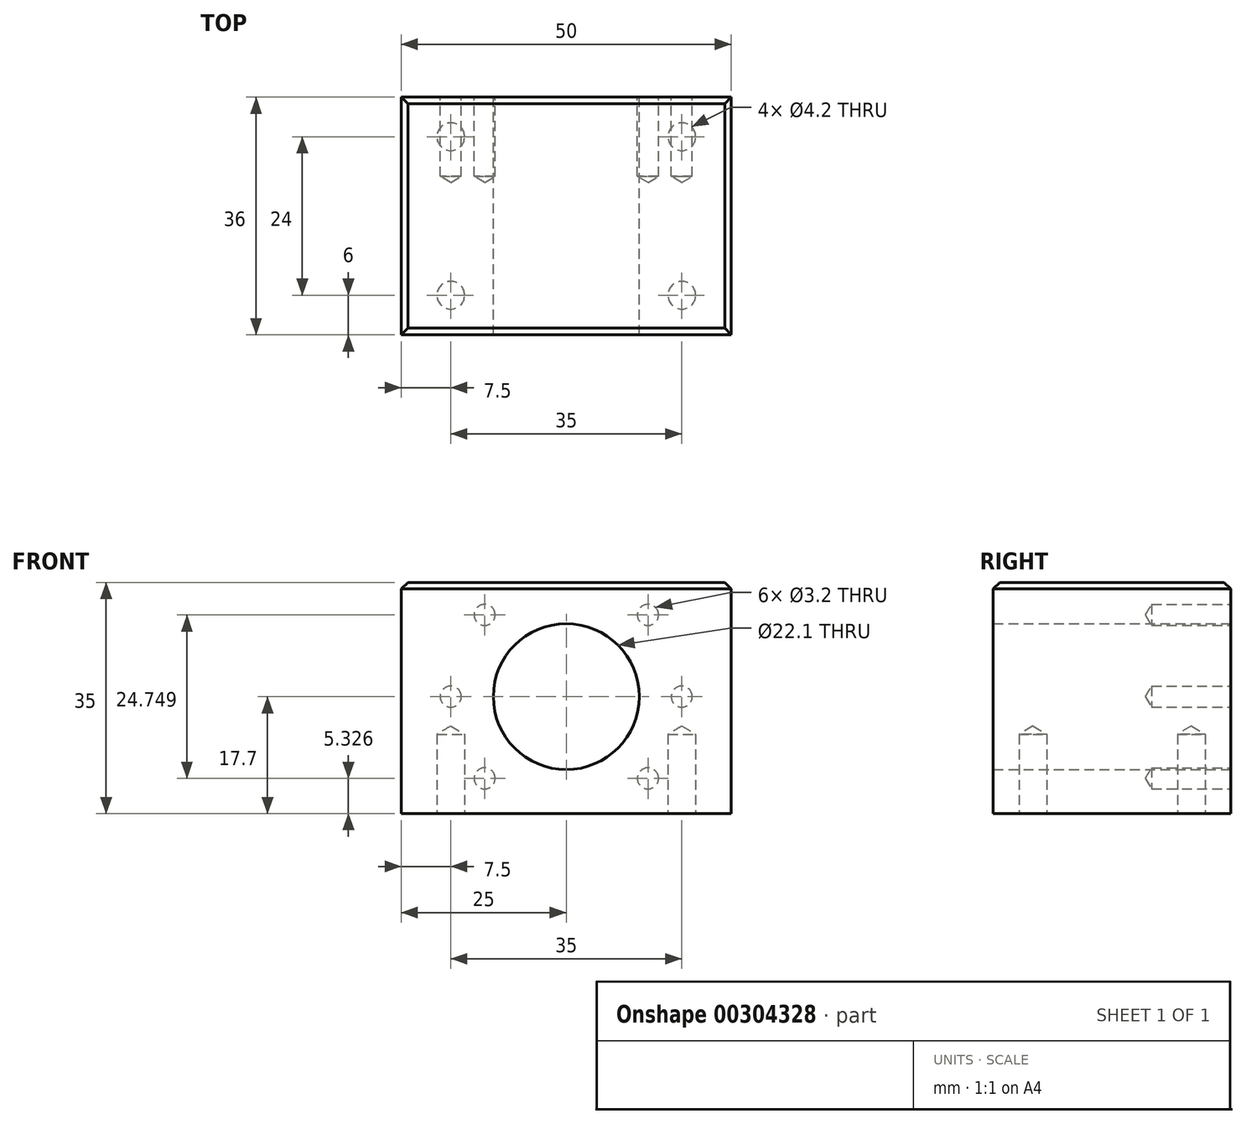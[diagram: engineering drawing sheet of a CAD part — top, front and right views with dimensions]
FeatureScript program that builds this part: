
annotation { "Feature Type Name" : "Feature", "Feature Type Description" : "" }
export const myFeature = defineFeature(function(context is Context, id is Id, definition is map)
    precondition{}
    {
        {
            var Q0;
            Q0=qCreatedBy(makeId("Front.planeOp"),FACE);
            var sketch = newSketch(context, id + "F0", { "sketchPlane" : qUnion([Q0])});
            skLineSegment(sketch, "E0", {"start": v(0, 12.9) * mm, "end": v(0, 0) * mm, "construction": true});
            skLineSegment(sketch, "E1", {"start": v(0, 0) * mm, "end": v(17.5, 0) * mm, "construction": true});
            skCircle(sketch, "E2", {"center": v(0, 0) * mm, "radius": 11.05 * mm});
            skLineSegment(sketch, "E3.bottom", {"start": v(-25, 17.3) * mm, "end": v(25, 17.3) * mm});
            skLineSegment(sketch, "E3.top", {"start": v(-25, -17.7) * mm, "end": v(25, -17.7) * mm});
            skLineSegment(sketch, "E3.left", {"start": v(-25, 17.3) * mm, "end": v(-25, -17.7) * mm});
            skLineSegment(sketch, "E3.right", {"start": v(25, 17.3) * mm, "end": v(25, -17.7) * mm});
            skCircle(sketch, "E4", {"center": v(0, 0) * mm, "radius": 17.5 * mm, "construction": true});
            skLineSegment(sketch, "E5", {"start": v(-12.37, 12.37) * mm, "end": v(0, 0) * mm, "construction": true});
            skLineSegment(sketch, "E6", {"start": v(0, 0) * mm, "end": v(-12.37, -12.37) * mm, "construction": true});
            skLineSegment(sketch, "E7", {"start": v(12.37, -12.37) * mm, "end": v(0, 0) * mm, "construction": true});
            skLineSegment(sketch, "E8", {"start": v(0, 0) * mm, "end": v(-17.5, 0) * mm, "construction": true});
            skLineSegment(sketch, "E9", {"start": v(12.37, 12.37) * mm, "end": v(0, 0) * mm, "construction": true});
            skPoint(sketch, "E10", {"position": v(-12.37, 12.37) * mm});
            skPoint(sketch, "E11", {"position": v(-17.5, 0) * mm});
            skPoint(sketch, "E12", {"position": v(-12.37, -12.37) * mm});
            skPoint(sketch, "E13", {"position": v(12.37, -12.37) * mm});
            skPoint(sketch, "E14", {"position": v(17.5, 0) * mm});
            skPoint(sketch, "E15", {"position": v(12.37, 12.37) * mm});
            skSolve(sketch);
        }
        {
            var Q0;
            Q0 = qSketchRegion(id + "F0", true);
            extrude(context, id + "F1", {"entities" : qUnion([Q0]), "depth" : 36 * mm});
        }
        {
            var Q0;
            Q0=sQuery(id+"F0.wireOp",VERTEX,"E10");
            var Q1;
            Q1=sQuery(id+"F0.wireOp",VERTEX,"E11");
            var Q2;
            Q2=sQuery(id+"F0.wireOp",VERTEX,"E12");
            var Q3;
            Q3=sQuery(id+"F0.wireOp",VERTEX,"E13");
            var Q4;
            Q4=sQuery(id+"F0.wireOp",VERTEX,"E14");
            var Q5;
            Q5=sQuery(id+"F0.wireOp",VERTEX,"E15");
            var Q6;
            Q6=makeQuery(id+"F1.opExtrude","SWEPT_BODY",BODY,{"disambiguationData":[OSD([sQuery(id+"F0.wireOp",EDGE,"E2"),sQuery(id+"F0.wireOp",EDGE,"E3.bottom"),sQuery(id+"F0.wireOp",EDGE,"E3.top"),sQuery(id+"F0.wireOp",EDGE,"E3.left"),sQuery(id+"F0.wireOp",EDGE,"E3.right")])]});
            hole(context, id + "F2", {"style" : HoleStyle.SIMPLE, "endStyle" : HoleEndStyle.BLIND, "oppositeDirection" : true, "standardTappedOrClearance" : lookupTablePath({ "standard" : "ISO", "engagement" : "75%", "pitch" : "0.75 mm", "size" : "M4", "type" : "Tapped" }), "standardBlindInLast" : lookupTablePath({ "standard" : "ISO", "engagement" : "75%", "pitch" : "0.75 mm", "size" : "M4", "type" : "Tapped" }), "holeDiameter" : 3.2 * mm, "showTappedDepth" : true, "holeDepth" : 12 * mm, "tappedDepth" : 9.75 * mm, "tapClearance" : 3, "locations" : qUnion([Q0, Q1, Q2, Q3, Q4, Q5]), "scope" : qUnion([Q6])});
        }
        {
            var Q0;
            Q0=makeQuery(id+"F1.opExtrude","SWEPT_EDGE",EDGE,{"disambiguationData":[OSD([sQuery(id+"F0.wireOp",EDGE,"E3.bottom"),sQuery(id+"F0.wireOp",EDGE,"E3.right")])]});
            var Q1;
            Q1=makeQuery(id+"F1.opExtrude","CAP_EDGE",EDGE,{"disambiguationData":[OSD([sQuery(id+"F0.wireOp",EDGE,"E3.bottom")])],"isStart":true});
            var Q2;
            Q2=makeQuery(id+"F1.opExtrude","SWEPT_EDGE",EDGE,{"disambiguationData":[OSD([sQuery(id+"F0.wireOp",EDGE,"E3.bottom"),sQuery(id+"F0.wireOp",EDGE,"E3.left")])]});
            var Q3;
            Q3=makeQuery(id+"F1.opExtrude","CAP_EDGE",EDGE,{"disambiguationData":[OSD([sQuery(id+"F0.wireOp",EDGE,"E3.bottom")])],"isStart":false});
            chamfer(context, id + "F3", {"entities" : qUnion([Q0, Q1, Q2, Q3]), "width" : 1 * mm, "tangentPropagation" : true});
        }
        {
            var Q0;
            Q0=makeQuery(id+"F1.opExtrude","SWEPT_FACE",FACE,{"disambiguationData":[OSD([sQuery(id+"F0.wireOp",EDGE,"E3.top")])]});
            var sketch = newSketch(context, id + "F4", { "sketchPlane" : qUnion([Q0])});
            skLineSegment(sketch, "E16.bottom", {"start": v(17.5, 6) * mm, "end": v(-17.5, 6) * mm, "construction": true});
            skLineSegment(sketch, "E16.top", {"start": v(17.5, 30) * mm, "end": v(-17.5, 30) * mm, "construction": true});
            skLineSegment(sketch, "E16.left", {"start": v(17.5, 6) * mm, "end": v(17.5, 30) * mm, "construction": true});
            skLineSegment(sketch, "E16.right", {"start": v(-17.5, 6) * mm, "end": v(-17.5, 30) * mm, "construction": true});
            skLineSegment(sketch, "E17", {"start": v(0, 0) * mm, "end": v(0, 36) * mm, "construction": true});
            skLineSegment(sketch, "E18", {"start": v(-25, 18) * mm, "end": v(25, 18) * mm, "construction": true});
            skPoint(sketch, "E19", {"position": v(17.5, 6) * mm});
            skPoint(sketch, "E20", {"position": v(-17.5, 6) * mm});
            skPoint(sketch, "E21", {"position": v(-17.5, 30) * mm});
            skPoint(sketch, "E22", {"position": v(17.5, 30) * mm});
            skSolve(sketch);
        }
        {
            var Q0;
            Q0=sQuery(id+"F4.wireOp",VERTEX,"E19");
            var Q1;
            Q1=sQuery(id+"F4.wireOp",VERTEX,"E22");
            var Q2;
            Q2=sQuery(id+"F4.wireOp",VERTEX,"E21");
            var Q3;
            Q3=sQuery(id+"F4.wireOp",VERTEX,"E20");
            var Q4;
            Q4=makeQuery(id+"F1.opExtrude","SWEPT_BODY",BODY,{"disambiguationData":[OSD([sQuery(id+"F0.wireOp",EDGE,"E2"),sQuery(id+"F0.wireOp",EDGE,"E3.bottom"),sQuery(id+"F0.wireOp",EDGE,"E3.top"),sQuery(id+"F0.wireOp",EDGE,"E3.left"),sQuery(id+"F0.wireOp",EDGE,"E3.right")])]});
            hole(context, id + "F5", {"style" : HoleStyle.SIMPLE, "endStyle" : HoleEndStyle.BLIND, "standardTappedOrClearance" : lookupTablePath({ "standard" : "ISO", "engagement" : "75%", "pitch" : "0.8 mm", "size" : "M5", "type" : "Tapped" }), "standardBlindInLast" : lookupTablePath({ "standard" : "ISO", "engagement" : "75%", "pitch" : "0.8 mm", "size" : "M5", "type" : "Tapped" }), "holeDiameter" : 4.2 * mm, "showTappedDepth" : true, "holeDepth" : 12 * mm, "tappedDepth" : 9.6 * mm, "tapClearance" : 3, "locations" : qUnion([Q0, Q1, Q2, Q3]), "scope" : qUnion([Q4]), "majorDiameter" : 5 * mm});
        }
    });
